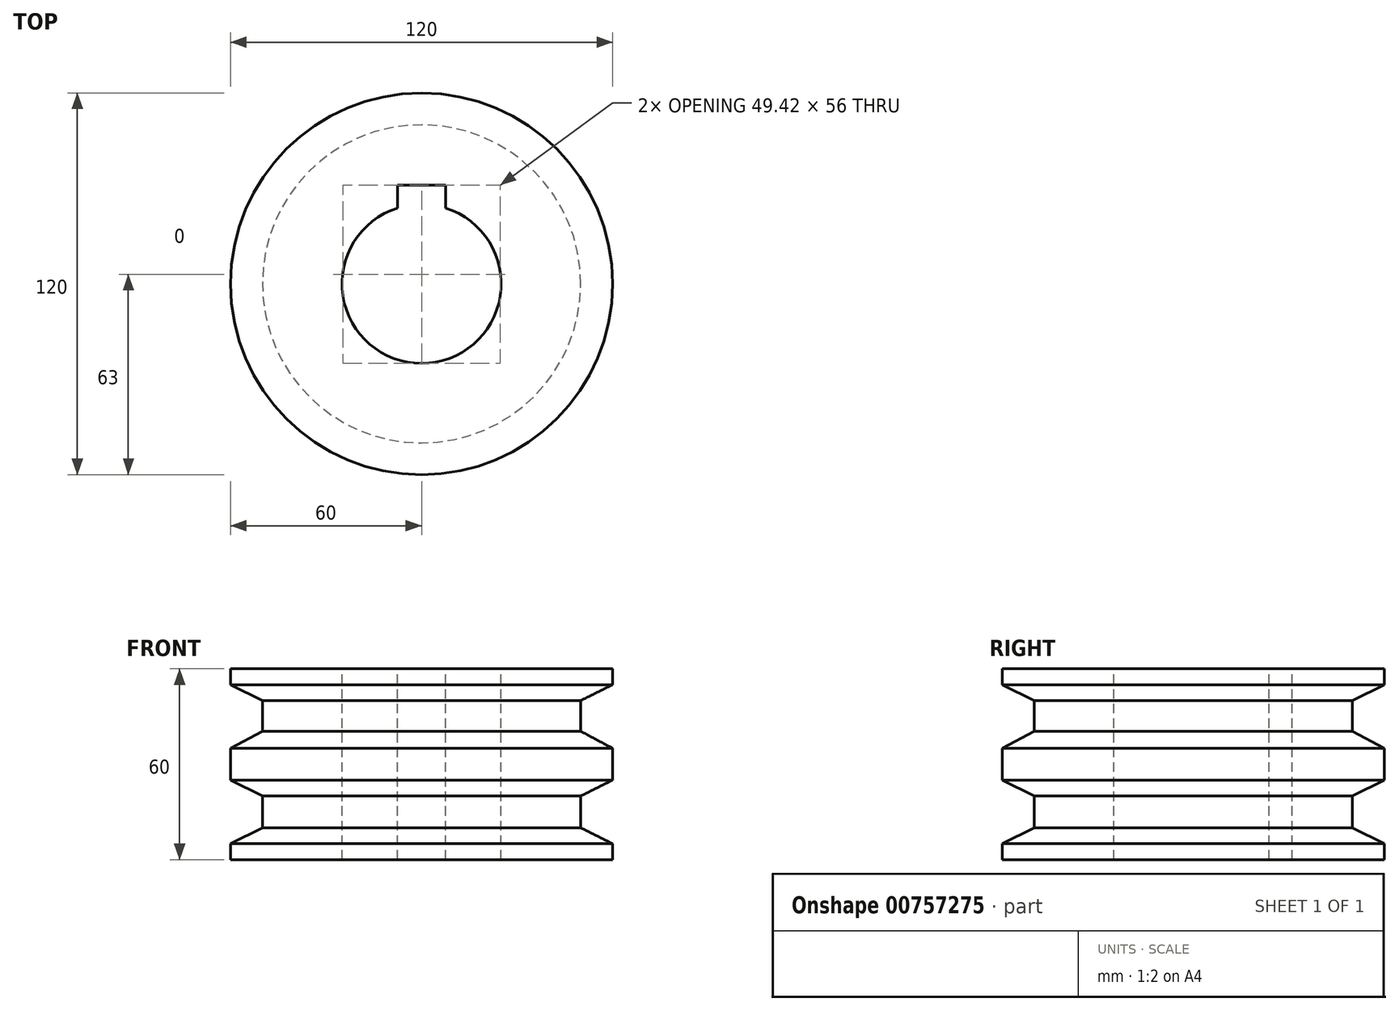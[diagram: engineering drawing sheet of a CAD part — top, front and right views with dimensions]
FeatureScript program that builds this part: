
annotation { "Feature Type Name" : "Feature", "Feature Type Description" : "" }
export const myFeature = defineFeature(function(context is Context, id is Id, definition is map)
    precondition{}
    {
        {
            var Q0;
            Q0=qCreatedBy(makeId("Front.planeOp"),FACE);
            var sketch = newSketch(context, id + "F0", { "sketchPlane" : qUnion([Q0])});
            skLineSegment(sketch, "E0.bottom", {"start": v(0, 30) * mm, "end": v(40, 30) * mm});
            skLineSegment(sketch, "E0.top", {"start": v(0, -30) * mm, "end": v(40, -30) * mm});
            skPoint(sketch, "E0.middle", {"position": v(0, 0) * mm});
            skLineSegment(sketch, "E1", {"start": v(40, 30) * mm, "end": v(50, 30) * mm});
            skLineSegment(sketch, "E2", {"start": v(50, 20) * mm, "end": v(50, 10) * mm});
            skLineSegment(sketch, "E3", {"start": v(50, -30) * mm, "end": v(40, -30) * mm});
            skPoint(sketch, "E4", {"position": v(50, 10) * mm});
            skPoint(sketch, "E5", {"position": v(50, -10) * mm});
            skPoint(sketch, "E6", {"position": v(50, -20) * mm});
            skPoint(sketch, "E7", {"position": v(50, 20) * mm});
            skLineSegment(sketch, "E8", {"start": v(50, 30) * mm, "end": v(60, 30) * mm});
            skLineSegment(sketch, "E9", {"start": v(60, 30) * mm, "end": v(60, 25) * mm});
            skLineSegment(sketch, "E10", {"start": v(60, -30) * mm, "end": v(50, -30) * mm});
            skPoint(sketch, "E11", {"position": v(60, 5) * mm});
            skPoint(sketch, "E12", {"position": v(60, 25) * mm});
            skPoint(sketch, "E13", {"position": v(60, -5) * mm});
            skPoint(sketch, "E14", {"position": v(60, -25) * mm});
            skLineSegment(sketch, "E15", {"start": v(50, 20) * mm, "end": v(60, 25) * mm});
            skLineSegment(sketch, "E16", {"start": v(50, 10.34) * mm, "end": v(60, 5) * mm});
            skLineSegment(sketch, "E17", {"start": v(50, -10) * mm, "end": v(60, -5) * mm});
            skLineSegment(sketch, "E18", {"start": v(50, -20) * mm, "end": v(60, -25) * mm});
            skLineSegment(sketch, "E19.trimOffspring", {"start": v(50, -10) * mm, "end": v(50, -20) * mm});
            skLineSegment(sketch, "E20.trimOffspring", {"start": v(60, -25) * mm, "end": v(60, -30) * mm});
            skLineSegment(sketch, "E21.trimOffspring", {"start": v(60, 5) * mm, "end": v(60, -5) * mm});
            skLineSegment(sketch, "E22", {"start": v(0, 30) * mm, "end": v(0, -30) * mm});
            skPoint(sketch, "E23", {"position": v(25, 30) * mm});
            skLineSegment(sketch, "E24", {"start": v(25, 30) * mm, "end": v(25, -30) * mm});
            skSolve(sketch);
        }
        {
            var Q0;
            {var subQ6=sQuery(id+"F0.wireOp",EDGE,"E1");Q0=makeQuery(id+"F0.imprint","IMPRINT",FACE,{"disambiguationData":[TD([[makeQuery(id+"F0.imprint","IMPRINT",EDGE,{"derivedFrom":subQ6}),-1.0]])]});}
            var Q1;
            Q1=sQuery(id+"F0.wireOp",EDGE,"E22");
            revolve(context, id + "F1", {"surfaceOperationType" : NewSurfaceOperationType.NEW, "entities" : qUnion([Q0]), "axis" : qUnion([Q1]), "revolveType" : RevolveType.FULL});
        }
        {
            var Q0;
            Q0=makeQuery(id+"F1.opRevolve","SWEPT_FACE",FACE,{"disambiguationData":[OSD([sQuery(id+"F0.wireOp",EDGE,"E0.bottom"),sQuery(id+"F0.wireOp",EDGE,"E1"),sQuery(id+"F0.wireOp",EDGE,"E8")])]});
            var sketch = newSketch(context, id + "F2", { "sketchPlane" : qUnion([Q0])});
            skLineSegment(sketch, "E25.top", {"start": v(-7.5, 31) * mm, "end": v(7.5, 31) * mm});
            skLineSegment(sketch, "E25.left", {"start": v(-7.5, 23.85) * mm, "end": v(-7.5, 31) * mm});
            skLineSegment(sketch, "E25.right", {"start": v(7.5, 23.85) * mm, "end": v(7.5, 31) * mm});
            skPoint(sketch, "E25.middle", {"position": v(0, 25) * mm});
            skPoint(sketch, "E26", {"position": v(-7.5, 23.85) * mm});
            skPoint(sketch, "E27", {"position": v(7.5, 23.85) * mm});
            skSolve(sketch);
        }
        {
            var Q0;
            Q0=makeQuery(id+"F2.imprint","IMPRINT",FACE,{"disambiguationData":[TD([[makeQuery(id+"F2.imprint","IMPRINT",EDGE,{"derivedFrom":sQuery(id+"F2.wireOp",EDGE,"E25.top")}),-1.0]])]});
            extrude(context, id + "F3", {"entities" : qUnion([Q0]), "operationType" : NewBodyOperationType.REMOVE, "endBound" : BoundingType.THROUGH_ALL, "oppositeDirection" : true, "depth" : 60 * mm, "offsetDistance" : 25 * mm});
        }
    });
